# Revit family: Vent Duct Wrap
name_source: partatom
category: Specialty Equipment
revit_build: Autodesk Revit 2015 (Build: 20160512_0715(x64)
units: mm (PartAtom-declared; Revit-internal decimal feet)

## types (7) — shared parameters
Conduit Material Suitability = HDEP, UPVC, PVC,
Description = FireFly 109 Vent Duct Wrap
IFC Classification = Building Element Proxy
Length_Calc = 100 mm  [stored 0.328084 ft]
Manufacturer = Tenmat ltd
Material = Intumescent Sealant
Performance = BS EN 1366-3:2009 & BS 476, ETA-12/0332, 1224-CPR-0341, CE Marked
URL = https://www.tenmat.com

## per-type parameters (varying)
| type | Height | Length | Width |
| Duct size - 110 x 54 | 54 mm  [stored 0.177165 ft] | 100 mm  [stored 0.328084 ft] | 110 mm  [stored 0.360892 ft] |
| Duct size - 204 x 60 | 60 mm  [stored 0.19685 ft] | 210 mm  [stored 0.688976 ft] | 204 mm |
| Duct size - 215 x 25 | 90 mm  [stored 0.295276 ft] | 210 mm  [stored 0.688976 ft] | 220 mm  [stored 0.721785 ft] |
| Duct size - 234 x 29 | 29 mm  [stored 0.0951444 ft] | 100 mm  [stored 0.328084 ft] | 234 mm  [stored 0.767717 ft] |
| Duct size - 308 x 29 | 29 mm  [stored 0.0951444 ft] | 100 mm  [stored 0.328084 ft] | 308 mm  [stored 1.0105 ft] |
| Duct size - 180 x 90 | 90 mm  [stored 0.295276 ft] | 100 mm  [stored 0.328084 ft] | 180 mm  [stored 0.590551 ft] |
| Duct size - 150 x 70 | 70 mm  [stored 0.229659 ft] | 100 mm  [stored 0.328084 ft] | 150 mm |

note: [stored X ft] marks values corroborated as IEEE doubles in the binary element streams (Revit-internal decimal feet)

## geometry (parser evidence)
native form markers: Blend x4, Sweep x1
no freeform markers — native parametric forms only
